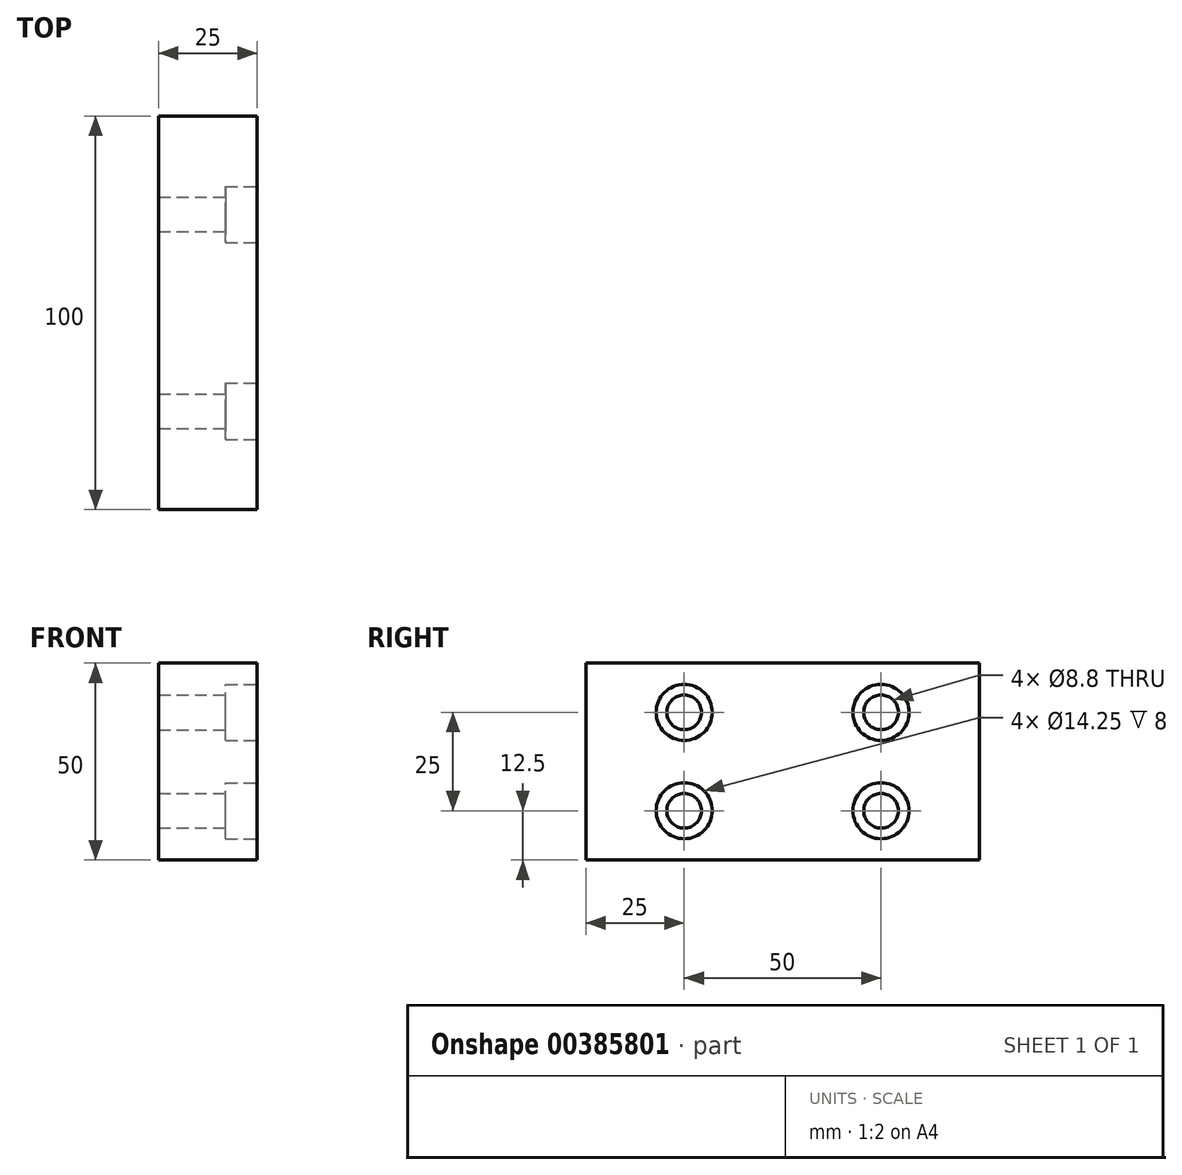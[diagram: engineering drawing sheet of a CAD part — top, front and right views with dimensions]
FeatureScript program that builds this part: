
annotation { "Feature Type Name" : "Feature", "Feature Type Description" : "" }
export const myFeature = defineFeature(function(context is Context, id is Id, definition is map)
    precondition{}
    {
        {
            var Q0;
            Q0=qCreatedBy(makeId("Right.planeOp"),FACE);
            var sketch = newSketch(context, id + "F0", { "sketchPlane" : qUnion([Q0])});
            skLineSegment(sketch, "E0.bottom", {"start": v(50, 25) * mm, "end": v(-50, 25) * mm});
            skLineSegment(sketch, "E0.top", {"start": v(50, -25) * mm, "end": v(-50, -25) * mm});
            skLineSegment(sketch, "E0.left", {"start": v(50, 25) * mm, "end": v(50, -25) * mm});
            skLineSegment(sketch, "E0.right", {"start": v(-50, 25) * mm, "end": v(-50, -25) * mm});
            skPoint(sketch, "E0.middle", {"position": v(0, 0) * mm});
            skSolve(sketch);
        }
        {
            var Q0;
            Q0=makeQuery(id+"F0.imprint","IMPRINT",FACE,{"disambiguationData":[TD([[makeQuery(id+"F0.imprint","IMPRINT",EDGE,{"derivedFrom":sQuery(id+"F0.wireOp",EDGE,"E0.bottom")}),1.0]])]});
            extrude(context, id + "F1", {"entities" : qUnion([Q0]), "endBound" : BoundingType.SYMMETRIC, "depth" : 25 * mm});
        }
        {
            var Q0;
            Q0=makeQuery(id+"F1.opExtrude","CAP_FACE",FACE,{"disambiguationData":[OSD([sQuery(id+"F0.wireOp",EDGE,"E0.bottom"),sQuery(id+"F0.wireOp",EDGE,"E0.top"),sQuery(id+"F0.wireOp",EDGE,"E0.left"),sQuery(id+"F0.wireOp",EDGE,"E0.right")])],"isStart":false});
            var sketch = newSketch(context, id + "F2", { "sketchPlane" : qUnion([Q0])});
            skPoint(sketch, "E1", {"position": v(-25, 12.5) * mm});
            skPoint(sketch, "E2", {"position": v(25, 12.5) * mm});
            skPoint(sketch, "E3", {"position": v(25, -12.5) * mm});
            skPoint(sketch, "E4", {"position": v(-25, -12.5) * mm});
            skSolve(sketch);
        }
        {
            var Q0;
            Q0=sQuery(id+"F2.wireOp",VERTEX,"E1");
            var Q1;
            Q1=sQuery(id+"F2.wireOp",VERTEX,"E4");
            var Q2;
            Q2=sQuery(id+"F2.wireOp",VERTEX,"E3");
            var Q3;
            Q3=sQuery(id+"F2.wireOp",VERTEX,"E2");
            var Q4;
            Q4=makeQuery(id+"F1.opExtrude","SWEPT_BODY",BODY,{"disambiguationData":[OSD([sQuery(id+"F0.wireOp",EDGE,"E0.bottom"),sQuery(id+"F0.wireOp",EDGE,"E0.top"),sQuery(id+"F0.wireOp",EDGE,"E0.left"),sQuery(id+"F0.wireOp",EDGE,"E0.right")])]});
            hole(context, id + "F3", {"style" : HoleStyle.C_BORE, "endStyle" : HoleEndStyle.THROUGH, "standardTappedOrClearance" : lookupTablePath({ "standard" : "ISO", "fit" : "Normal", "size" : "M8", "type" : "Clearance" }), "standardBlindInLast" : lookupTablePath({ "fit" : "Standard", "standard" : "ISO", "size" : "M8", "type" : "Clearance" }), "holeDiameter" : 8.8 * mm, "cBoreDiameter" : 14.25 * mm, "cBoreDepth" : 8 * mm, "isTappedThrough" : true, "tappedDepth" : 12 * mm, "tapClearance" : 3, "locations" : qUnion([Q0, Q1, Q2, Q3]), "scope" : qUnion([Q4])});
        }
    });
